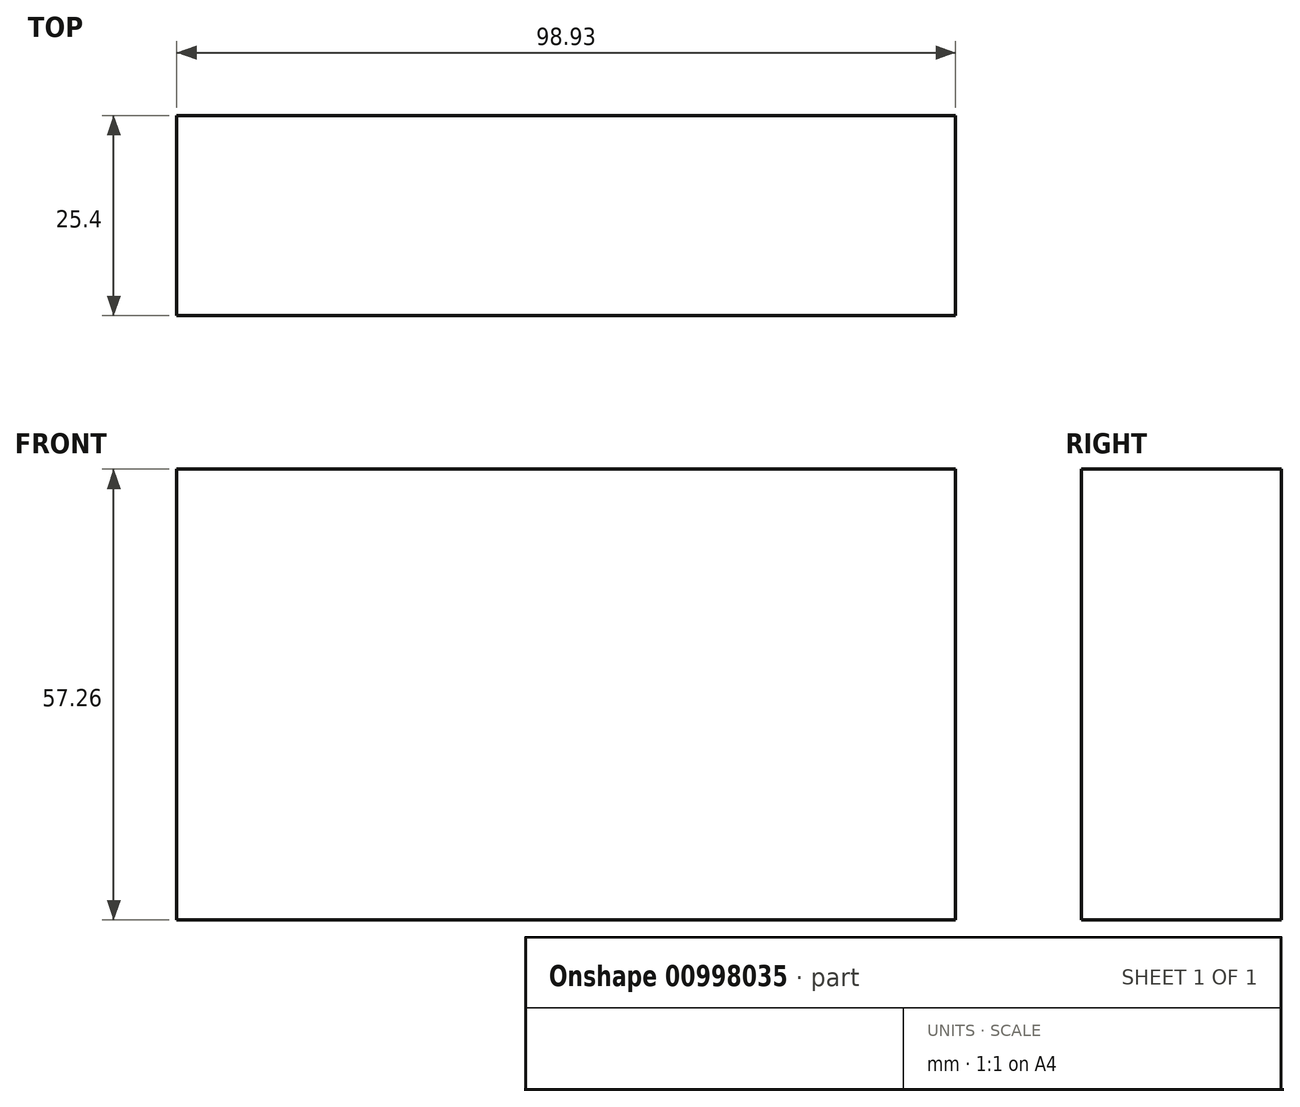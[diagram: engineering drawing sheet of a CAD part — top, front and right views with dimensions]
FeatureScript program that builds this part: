
annotation { "Feature Type Name" : "Feature", "Feature Type Description" : "" }
export const myFeature = defineFeature(function(context is Context, id is Id, definition is map)
    precondition{}
    {
        {
            var Q0;
            Q0=qCreatedBy(makeId("Front.planeOp"),FACE);
            var sketch = newSketch(context, id + "F0", { "sketchPlane" : qUnion([Q0])});
            skLineSegment(sketch, "E0.bottom", {"start": v(26.6, 57.26) * mm, "end": v(125.52, 57.26) * mm});
            skLineSegment(sketch, "E0.top", {"start": v(26.6, 0) * mm, "end": v(125.52, 0) * mm});
            skLineSegment(sketch, "E0.left", {"start": v(26.6, 57.26) * mm, "end": v(26.6, 0) * mm});
            skLineSegment(sketch, "E0.right", {"start": v(125.52, 57.26) * mm, "end": v(125.52, 0) * mm});
            skSolve(sketch);
        }
        {
            var Q0;
            Q0 = qSketchRegion(id + "F0", true);
            extrude(context, id + "F1", {"entities" : qUnion([Q0]), "depth" : 25.4 * mm, "offsetDistance" : 25.4 * mm});
        }
    });
